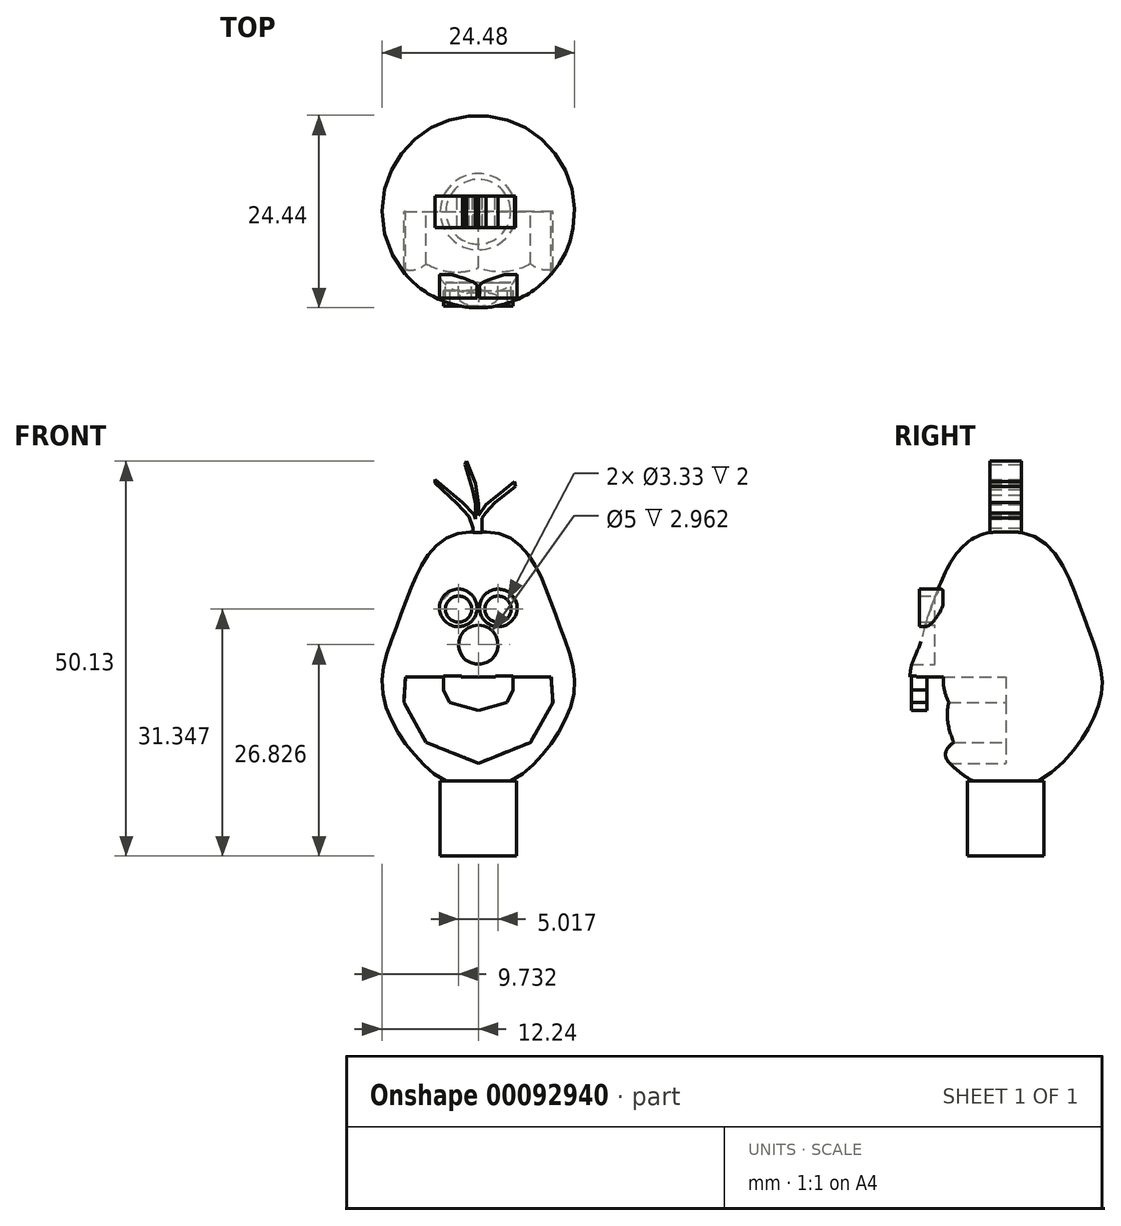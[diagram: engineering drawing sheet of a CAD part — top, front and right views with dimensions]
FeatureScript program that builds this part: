
annotation { "Feature Type Name" : "Feature", "Feature Type Description" : "" }
export const myFeature = defineFeature(function(context is Context, id is Id, definition is map)
    precondition{}
    {
        {
            var Q0;
            Q0=qCreatedBy(makeId("Top.planeOp"),FACE);
            cPlane(context, id + "F0", {"entities" : qUnion([Q0]), "cplaneType" : CPlaneType.OFFSET, "offset" : 10 * mm, "oppositeDirection" : true, "width" : 152.4 * mm, "height" : 152.4 * mm});
        }
        {
            var Q0;
            Q0=qCreatedBy(id+"F0.planeOp",FACE);
            var sketch = newSketch(context, id + "F1", { "sketchPlane" : qUnion([Q0])});
            skCircle(sketch, "E0", {"center": v(0, 0) * mm, "radius": 4.85 * mm});
            skSolve(sketch);
        }
        {
            var Q0;
            Q0 = qSketchRegion(id + "F1", true);
            extrude(context, id + "F2", {"entities" : qUnion([Q0]), "oppositeDirection" : true, "depth" : 9.5 * mm});
        }
        {
            var Q0;
            Q0=qCreatedBy(makeId("Front.planeOp"),FACE);
            var sketch = newSketch(context, id + "F3", { "sketchPlane" : qUnion([Q0])});
            skFitSpline(sketch, "E1", {"points": [v(0, -9.97) * mm, v(-4.17, -9.97) * mm, v(-11.9, 0) * mm, v(-9.87, 10.99) * mm, v(0, 21.57) * mm], "startDerivative": vector(-25.28, -6.57) * mm, "endDerivative": vector(62.37, -8.18) * mm});
            skLineSegment(sketch, "E2", {"start": v(0, 21.57) * mm, "end": v(0, -9.97) * mm});
            skSolve(sketch);
        }
        {
            var Q0;
            Q0=makeQuery(id+"F3.imprint","IMPRINT",FACE,{"disambiguationData":[TD([[makeQuery(id+"F3.imprint","IMPRINT",EDGE,{"derivedFrom":sQuery(id+"F3.wireOp",EDGE,"E1")}),-1.0]])]});
            var Q1;
            Q1=sQuery(id+"F3.wireOp",EDGE,"E2");
            revolve(context, id + "F4", {"operationType" : NewBodyOperationType.ADD, "entities" : qUnion([Q0]), "axis" : qUnion([Q1]), "revolveType" : RevolveType.FULL});
        }
        {
            var Q0;
            Q0=qCreatedBy(makeId("Front.planeOp"),FACE);
            cPlane(context, id + "F5", {"entities" : qUnion([Q0]), "cplaneType" : CPlaneType.OFFSET, "offset" : 9 * mm, "width" : 150 * mm, "height" : 150 * mm});
        }
        {
            var Q0;
            Q0=qCreatedBy(id+"F5.planeOp",FACE);
            var sketch = newSketch(context, id + "F6", { "sketchPlane" : qUnion([Q0])});
            skCircle(sketch, "E3", {"center": v(0, 7.33) * mm, "radius": 2.5 * mm});
            skSolve(sketch);
        }
        {
            var Q0;
            Q0 = qSketchRegion(id + "F6", true);
            extrude(context, id + "F7", {"entities" : qUnion([Q0]), "operationType" : NewBodyOperationType.REMOVE, "depth" : 5 * mm});
        }
        {
            var Q0;
            Q0=qCreatedBy(id+"F5.planeOp",FACE);
            var sketch = newSketch(context, id + "F8", { "sketchPlane" : qUnion([Q0])});
            skCircle(sketch, "E4", {"center": v(-2.54, 12) * mm, "radius": 2.38 * mm});
            skCircle(sketch, "E5.MirrorC", {"center": v(2.54, 12) * mm, "radius": 2.38 * mm});
            skSolve(sketch);
        }
        {
            var Q0;
            Q0 = qSketchRegion(id + "F8", true);
            extrude(context, id + "F9", {"entities" : qUnion([Q0]), "operationType" : NewBodyOperationType.ADD, "depth" : 2 * mm});
        }
        {
            var Q0;
            Q0 = qSketchRegion(id + "F8", true);
            extrude(context, id + "F10", {"entities" : qUnion([Q0]), "operationType" : NewBodyOperationType.ADD, "oppositeDirection" : true, "depth" : 1 * mm});
        }
        {
            var Q0;
            Q0=qCreatedBy(id+"F5.planeOp",FACE);
            var sketch = newSketch(context, id + "F11", { "sketchPlane" : qUnion([Q0])});
            skCircle(sketch, "E6", {"center": v(-2.5, 11.85) * mm, "radius": 1.66 * mm});
            skCircle(sketch, "E7.MirrorC", {"center": v(2.5, 11.85) * mm, "radius": 1.66 * mm});
            skSolve(sketch);
        }
        {
            var Q0;
            Q0 = qSketchRegion(id + "F11", true);
            extrude(context, id + "F12", {"entities" : qUnion([Q0]), "operationType" : NewBodyOperationType.REMOVE, "depth" : 10 * mm});
        }
        {
            var Q0;
            Q0=qCreatedBy(makeId("Front.planeOp"),FACE);
            var sketch = newSketch(context, id + "F13", { "sketchPlane" : qUnion([Q0])});
            skLineSegment(sketch, "E8", {"start": v(-8.65, 3.26) * mm, "end": v(9.26, 3.26) * mm});
            skLineSegment(sketch, "E9", {"start": v(9.26, 3.26) * mm, "end": v(9.46, 0) * mm});
            skLineSegment(sketch, "E10", {"start": v(9.46, 0) * mm, "end": v(6.61, -5.09) * mm});
            skLineSegment(sketch, "E11", {"start": v(6.61, -5.09) * mm, "end": v(0, -7.73) * mm});
            skLineSegment(sketch, "E12.MirrorCS", {"start": v(-9.46, 0) * mm, "end": v(-6.61, -5.09) * mm});
            skLineSegment(sketch, "E13.MirrorCS", {"start": v(-6.61, -5.09) * mm, "end": v(0, -7.73) * mm});
            skLineSegment(sketch, "E14.MirrorCS", {"start": v(8.65, 3.26) * mm, "end": v(-9.26, 3.26) * mm});
            skLineSegment(sketch, "E15.MirrorCS", {"start": v(-9.26, 3.26) * mm, "end": v(-9.46, 0) * mm});
            skSolve(sketch);
        }
        {
            var Q0;
            Q0 = qSketchRegion(id + "F13", true);
            extrude(context, id + "F14", {"entities" : qUnion([Q0]), "operationType" : NewBodyOperationType.REMOVE, "depth" : 13 * mm});
        }
        {
            var Q0;
            Q0=qCreatedBy(id+"F5.planeOp",FACE);
            cPlane(context, id + "F15", {"entities" : qUnion([Q0]), "cplaneType" : CPlaneType.OFFSET, "offset" : 3 * mm, "width" : 150 * mm, "height" : 150 * mm});
        }
        {
            var Q0;
            Q0=qCreatedBy(id+"F15.planeOp",FACE);
            var sketch = newSketch(context, id + "F16", { "sketchPlane" : qUnion([Q0])});
            skLineSegment(sketch, "E16", {"start": v(-4.4, 3.34) * mm, "end": v(0, 3.34) * mm});
            skLineSegment(sketch, "E17", {"start": v(0, 3.34) * mm, "end": v(0, -1.02) * mm});
            skLineSegment(sketch, "E18", {"start": v(0, -1.02) * mm, "end": v(-3.63, 0) * mm});
            skLineSegment(sketch, "E19", {"start": v(-3.63, 0) * mm, "end": v(-4.4, 1.55) * mm});
            skLineSegment(sketch, "E20", {"start": v(-4.4, 1.55) * mm, "end": v(-4.4, 3.34) * mm});
            skLineSegment(sketch, "E21.MirrorCS", {"start": v(4.4, 1.55) * mm, "end": v(4.4, 3.34) * mm});
            skLineSegment(sketch, "E22.MirrorCS", {"start": v(0, -1.02) * mm, "end": v(3.63, 0) * mm});
            skLineSegment(sketch, "E23.MirrorCS", {"start": v(3.63, 0) * mm, "end": v(4.4, 1.55) * mm});
            skLineSegment(sketch, "E24.MirrorCS", {"start": v(4.4, 3.34) * mm, "end": v(0, 3.34) * mm});
            skSolve(sketch);
        }
        {
            var Q0;
            Q0 = qSketchRegion(id + "F16", true);
            extrude(context, id + "F17", {"entities" : qUnion([Q0]), "operationType" : NewBodyOperationType.ADD, "oppositeDirection" : true, "depth" : 2 * mm});
        }
        {
            var Q0;
            Q0=qCreatedBy(makeId("Front.planeOp"),FACE);
            var sketch = newSketch(context, id + "F18", { "sketchPlane" : qUnion([Q0])});
            skLineSegment(sketch, "E25", {"start": v(-1.18, 23.62) * mm, "end": v(-2.7, 25.26) * mm});
            skLineSegment(sketch, "E26", {"start": v(-2.7, 25.26) * mm, "end": v(-5.53, 27.86) * mm});
            skLineSegment(sketch, "E27", {"start": v(-5.53, 27.86) * mm, "end": v(-5.53, 28.3) * mm});
            skLineSegment(sketch, "E28", {"start": v(-5.53, 28.3) * mm, "end": v(-1.98, 25.41) * mm});
            skLineSegment(sketch, "E29", {"start": v(-1.98, 25.41) * mm, "end": v(-0.54, 23.89) * mm});
            skLineSegment(sketch, "E30", {"start": v(-0.54, 23.89) * mm, "end": v(0, 22.21) * mm});
            skLineSegment(sketch, "E31", {"start": v(0, 22.21) * mm, "end": v(0, 21) * mm});
            skLineSegment(sketch, "E32", {"start": v(-1.18, 23.62) * mm, "end": v(-0.65, 22.17) * mm});
            skLineSegment(sketch, "E33", {"start": v(-0.65, 22.17) * mm, "end": v(-0.69, 20.91) * mm});
            skLineSegment(sketch, "E34", {"start": v(-0.69, 20.91) * mm, "end": v(0, 21) * mm});
            skLineSegment(sketch, "E35", {"start": v(-0.34, 20.95) * mm, "end": v(-0.34, 25.26) * mm});
            skLineSegment(sketch, "E36", {"start": v(-0.34, 25.26) * mm, "end": v(-0.73, 27.05) * mm});
            skLineSegment(sketch, "E37", {"start": v(-0.73, 27.05) * mm, "end": v(-1.72, 30.21) * mm});
            skLineSegment(sketch, "E38", {"start": v(-1.72, 30.21) * mm, "end": v(-1.49, 30.63) * mm});
            skLineSegment(sketch, "E39", {"start": v(-1.49, 30.63) * mm, "end": v(-0.35, 27.77) * mm});
            skLineSegment(sketch, "E40", {"start": v(-0.35, 27.77) * mm, "end": v(0, 25.22) * mm});
            skLineSegment(sketch, "E41", {"start": v(0, 25.22) * mm, "end": v(0, 21) * mm});
            skLineSegment(sketch, "E42", {"start": v(0, 21) * mm, "end": v(0, 23.74) * mm});
            skLineSegment(sketch, "E43", {"start": v(0, 23.74) * mm, "end": v(0.99, 25.1) * mm});
            skLineSegment(sketch, "E44", {"start": v(0.99, 25.1) * mm, "end": v(2.48, 26.36) * mm});
            skLineSegment(sketch, "E45", {"start": v(2.48, 26.36) * mm, "end": v(4.58, 28.04) * mm});
            skLineSegment(sketch, "E46", {"start": v(4.58, 28.04) * mm, "end": v(4.74, 27.45) * mm});
            skLineSegment(sketch, "E47", {"start": v(4.74, 27.45) * mm, "end": v(2.13, 25.41) * mm});
            skLineSegment(sketch, "E48", {"start": v(2.13, 25.41) * mm, "end": v(0.91, 24.08) * mm});
            skLineSegment(sketch, "E49", {"start": v(0.91, 24.08) * mm, "end": v(0.46, 23.4) * mm});
            skLineSegment(sketch, "E50", {"start": v(0.46, 23.4) * mm, "end": v(0.46, 20.88) * mm});
            skLineSegment(sketch, "E51", {"start": v(0.46, 20.88) * mm, "end": v(0, 21) * mm});
            skSolve(sketch);
        }
        {
            var Q0;
            Q0 = qSketchRegion(id + "F18", true);
            extrude(context, id + "F19", {"entities" : qUnion([Q0]), "operationType" : NewBodyOperationType.ADD, "depth" : 2 * mm});
        }
        {
            var Q0;
            Q0 = qSketchRegion(id + "F18", true);
            extrude(context, id + "F20", {"entities" : qUnion([Q0]), "operationType" : NewBodyOperationType.ADD, "oppositeDirection" : true, "depth" : 2 * mm});
        }
    });
